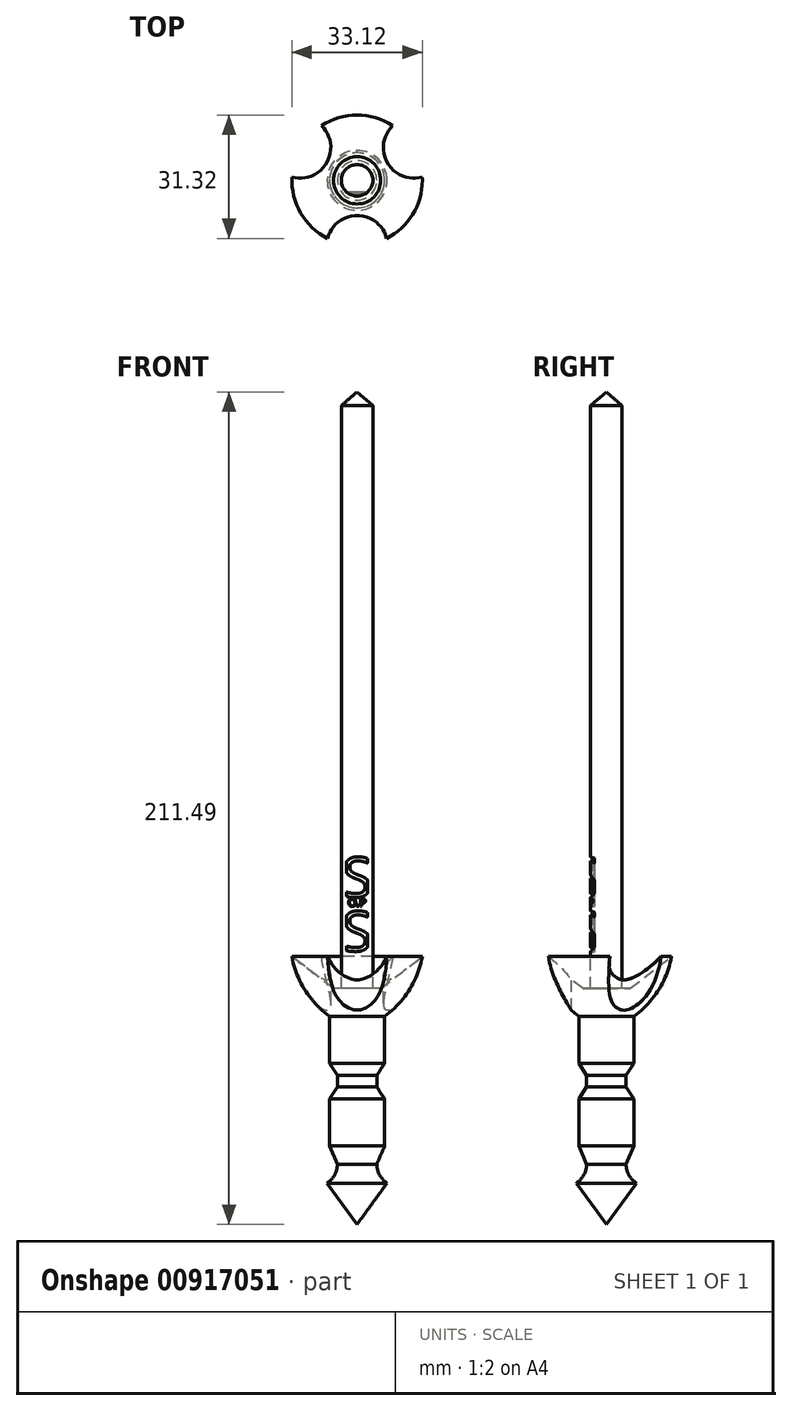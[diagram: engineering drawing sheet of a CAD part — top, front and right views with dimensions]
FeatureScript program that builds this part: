
annotation { "Feature Type Name" : "Feature", "Feature Type Description" : "" }
export const myFeature = defineFeature(function(context is Context, id is Id, definition is map)
    precondition{}
    {
        {
            var Q0;
            Q0=qCreatedBy(makeId("Front.planeOp"),FACE);
            var sketch = newSketch(context, id + "F0", { "sketchPlane" : qUnion([Q0])});
            skLineSegment(sketch, "E0", {"start": v(5, -107.92) * mm, "end": v(7, -103.34) * mm});
            skLineSegment(sketch, "E1", {"start": v(7, -103.34) * mm, "end": v(7, -91.34) * mm});
            skLineSegment(sketch, "E2", {"start": v(7, -91.34) * mm, "end": v(5, -88.34) * mm});
            skLineSegment(sketch, "E3", {"start": v(5, -88.34) * mm, "end": v(5, -85.34) * mm});
            skLineSegment(sketch, "E4", {"start": v(5, -85.34) * mm, "end": v(7, -82.34) * mm});
            skLineSegment(sketch, "E5", {"start": v(7, -82.34) * mm, "end": v(7, -70.34) * mm});
            skLineSegment(sketch, "E6", {"start": v(0, 84.78) * mm, "end": v(0, -115.22) * mm});
            skLineSegment(sketch, "E7", {"start": v(0, -115.22) * mm, "end": v(0, -123.22) * mm});
            skLineSegment(sketch, "E8", {"start": v(5, -107.92) * mm, "end": v(5, -107.92) * mm});
            skLineSegment(sketch, "E9", {"start": v(6, -63.32) * mm, "end": v(4, -63.32) * mm});
            skLineSegment(sketch, "E10", {"start": v(4, -63.32) * mm, "end": v(4, 84.78) * mm});
            skCircle(sketch, "E11.cCircle", {"center": v(5.5, -119.22) * mm, "radius": 6.8 * mm, "construction": true});
            skLineSegment(sketch, "E11.4", {"start": v(0, -123.22) * mm, "end": v(0, -115.22) * mm});
            skArc(sketch, "E12", {"start": v(5, -107.92) * mm, "mid": v(5.7, -110.66) * mm, "end": v(7.6, -112.75) * mm});
            skLineSegment(sketch, "E13", {"start": v(4, 84.78) * mm, "end": v(0, 88.27) * mm});
            skLineSegment(sketch, "E14", {"start": v(0, 88.27) * mm, "end": v(0, 84.78) * mm});
            skLineSegment(sketch, "E15", {"start": v(7.6, -112.75) * mm, "end": v(0, -123.22) * mm});
            skLineSegment(sketch, "E16", {"start": v(6, -63.32) * mm, "end": v(16.56, -55.2) * mm});
            skArc(sketch, "E17", {"start": v(7, -70.34) * mm, "mid": v(13.24, -63.69) * mm, "end": v(16.56, -55.2) * mm});
            skSolve(sketch);
        }
        {
            var Q0;
            {var subQ3=sQuery(id+"F0.wireOp",EDGE,"E1");Q0=makeQuery(id+"F0.imprint","IMPRINT",FACE,{"disambiguationData":[TD([[makeQuery(id+"F0.imprint","IMPRINT",EDGE,{"derivedFrom":subQ3}),1.0]])]});}
            var Q1;
            Q1=makeQuery(id+"F0.imprint","IMPRINT",FACE,{"disambiguationData":[TD([[makeQuery(id+"F0.imprint","IMPRINT",EDGE,{"derivedFrom":sQuery(id+"F0.wireOp",EDGE,"E7")}),1.0]])]});
            var Q2;
            Q2=sQuery(id+"F0.wireOp",EDGE,"E6");
            revolve(context, id + "F1", {"surfaceOperationType" : NewSurfaceOperationType.NEW, "entities" : qUnion([Q0, Q1]), "axis" : qUnion([Q2]), "revolveType" : RevolveType.FULL});
        }
        {
            var Q0;
            Q0=qCreatedBy(makeId("Front.planeOp"),FACE);
            var sketch = newSketch(context, id + "F2", { "sketchPlane" : qUnion([Q0])});
            skText(sketch, "E18", { "text": "S", "fontName": "OpenSans-Regular.ttf"});
            skText(sketch, "E19", { "text": "S", "fontName": "OpenSans-Regular.ttf"});
            skText(sketch, "E20", { "text": "O.P", "fontName": "OpenSans-Regular.ttf"});
            const initialGuessF2  = {"E18": [-0.00389, -0.04007, 1, 0, 0.01018], "E19": [-0.00389, -0.0538, 1, 0, 0.01018], "E20": [-0.00232, -0.04244, 1, 0, 0.002]};
            skSetInitialGuess(sketch, initialGuessF2);
            skSolve(sketch);
        }
        {
            var Q0;
            Q0 = qSketchRegion(id + "F2", true);
            var Q1;
            Q1 = qConstructionFilter(qBodyType(qCreatedBy(id + "F2" ,EDGE), BodyType.WIRE), ConstructionObject.NO);
            extrude(context, id + "F3", {"entities" : qUnion([Q0]), "operationType" : NewBodyOperationType.REMOVE, "surfaceEntities" : qUnion([Q1]), "depth" : 10 * mm, "offsetDistance" : 25 * mm, "hasSecondDirection" : true, "secondDirectionOppositeDirection" : false, "secondDirectionDepth" : 3 * mm});
        }
        {
            var Q0;
            Q0=qCreatedBy(makeId("Top.planeOp"),FACE);
            var sketch = newSketch(context, id + "F4", { "sketchPlane" : qUnion([Q0])});
            skCircle(sketch, "E21", {"center": v(0, -16.64) * mm, "radius": 7.74 * mm});
            skCircle(sketch, "E22.1.0", {"center": v(14.41, 8.32) * mm, "radius": 7.74 * mm});
            skCircle(sketch, "E22.2.0", {"center": v(-14.41, 8.32) * mm, "radius": 7.74 * mm});
            skPoint(sketch, "E22.center", {"position": v(0, 0) * mm});
            skSolve(sketch);
        }
        {
            var Q0;
            Q0=makeQuery(id+"F4.imprint","IMPRINT",FACE,{"disambiguationData":[TD([[makeQuery(id+"F4.imprint","IMPRINT",EDGE,{"derivedFrom":sQuery(id+"F4.wireOp",EDGE,"E21")}),1.0]])]});
            var Q1;
            Q1=makeQuery(id+"F4.imprint","IMPRINT",FACE,{"disambiguationData":[TD([[makeQuery(id+"F4.imprint","IMPRINT",EDGE,{"derivedFrom":sQuery(id+"F4.wireOp",EDGE,"E22.2.0")}),1.0]])]});
            var Q2;
            Q2=makeQuery(id+"F4.imprint","IMPRINT",FACE,{"disambiguationData":[TD([[makeQuery(id+"F4.imprint","IMPRINT",EDGE,{"derivedFrom":sQuery(id+"F4.wireOp",EDGE,"E22.1.0")}),1.0]])]});
            extrude(context, id + "F5", {"entities" : qUnion([Q0, Q1, Q2]), "operationType" : NewBodyOperationType.REMOVE, "oppositeDirection" : true, "depth" : 100 * mm, "offsetDistance" : 25 * mm});
        }
    });
